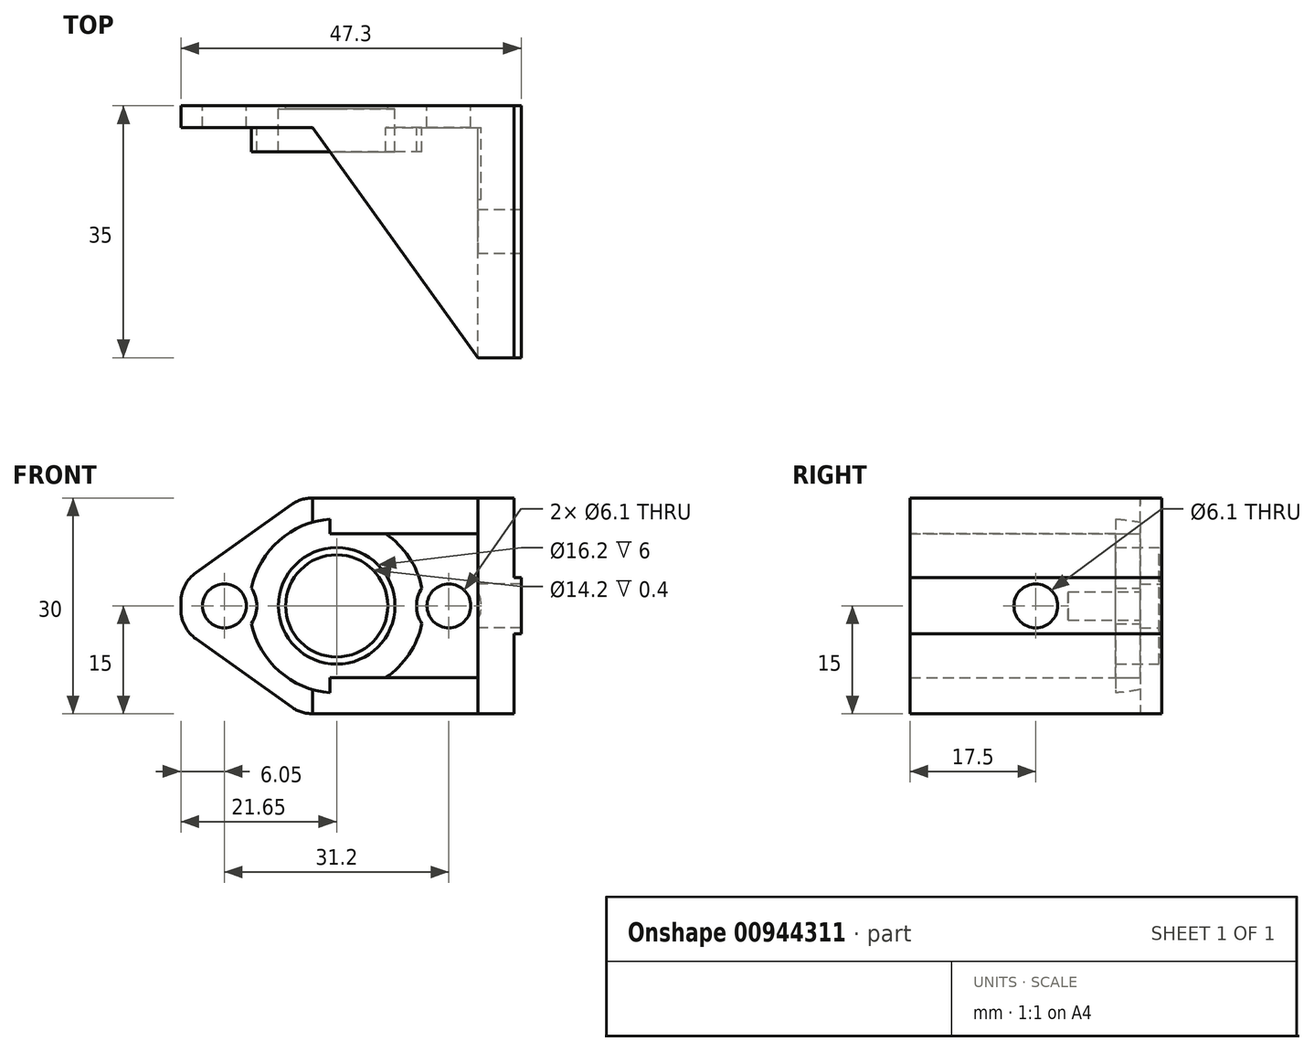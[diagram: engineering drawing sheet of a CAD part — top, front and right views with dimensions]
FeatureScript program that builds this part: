
annotation { "Feature Type Name" : "Feature", "Feature Type Description" : "" }
export const myFeature = defineFeature(function(context is Context, id is Id, definition is map)
    precondition{}
    {
        {
            var Q0;
            Q0=qCreatedBy(makeId("Front.planeOp"),FACE);
            var sketch = newSketch(context, id + "F0", { "sketchPlane" : qUnion([Q0])});
            skLineSegment(sketch, "E0.right", {"start": v(-21.65, -0.54) * mm, "end": v(-21.65, 0.54) * mm});
            skPoint(sketch, "E0.middle", {"position": v(0, 0) * mm});
            skCircle(sketch, "E1", {"center": v(-15.6, 0) * mm, "radius": 3.05 * mm});
            skCircle(sketch, "E2.MirrorC", {"center": v(15.6, 0) * mm, "radius": 3.05 * mm});
            skCircle(sketch, "E3", {"center": v(0, 0) * mm, "radius": 8.1 * mm});
            skCircle(sketch, "E4", {"center": v(0, 0) * mm, "radius": 12.1 * mm});
            skLineSegment(sketch, "E5", {"start": v(-17.37, 2.48) * mm, "end": v(-7.02, 9.86) * mm, "construction": true});
            skLineSegment(sketch, "E6", {"start": v(-19.55, 4.61) * mm, "end": v(-6.27, 14.07) * mm});
            skPoint(sketch, "E7.visualSharp", {"position": v(-21.65, 3.12) * mm});
            skArc(sketch, "E7.filletArc", {"start": v(-19.55, 4.61) * mm, "mid": v(-21.1, 2.83) * mm, "end": v(-21.65, 0.54) * mm});
            skArc(sketch, "E8.filletArc", {"start": v(-3.37, 15) * mm, "mid": v(-4.9, 14.76) * mm, "end": v(-6.27, 14.07) * mm});
            skArc(sketch, "E9.MirrorCS", {"start": v(-19.55, -4.61) * mm, "mid": v(-21.1, -2.83) * mm, "end": v(-21.65, -0.54) * mm});
            skLineSegment(sketch, "E10.MirrorCS", {"start": v(-19.55, -4.61) * mm, "end": v(-6.27, -14.07) * mm});
            skArc(sketch, "E11.MirrorCS", {"start": v(-3.37, -15) * mm, "mid": v(-4.9, -14.76) * mm, "end": v(-6.27, -14.07) * mm});
            skPoint(sketch, "E12.orphan", {"position": v(-21.65, -15) * mm});
            skLineSegment(sketch, "E13", {"start": v(-3.37, 15) * mm, "end": v(19.65, 15) * mm});
            skLineSegment(sketch, "E14", {"start": v(19.65, 15) * mm, "end": v(19.65, -15) * mm});
            skLineSegment(sketch, "E15", {"start": v(19.65, -15) * mm, "end": v(-3.37, -15) * mm});
            skLineSegment(sketch, "E16.bottom", {"start": v(19.65, 15) * mm, "end": v(24.65, 15) * mm});
            skLineSegment(sketch, "E16.top", {"start": v(19.65, -15) * mm, "end": v(24.65, -15) * mm});
            skLineSegment(sketch, "E16.right", {"start": v(24.65, 15) * mm, "end": v(24.65, -15) * mm});
            skSolve(sketch);
        }
        {
            var Q0;
            Q0=makeQuery(id+"F0.imprint","IMPRINT",FACE,{"disambiguationData":[TD([[makeQuery(id+"F0.imprint","IMPRINT",EDGE,{"derivedFrom":sQuery(id+"F0.wireOp",EDGE,"E3")}),-1.0]])]});
            extrude(context, id + "F1", {"entities" : qUnion([Q0]), "depth" : 6.4 * mm, "offsetDistance" : 25 * mm});
        }
        {
            var Q0;
            Q0=qSketchRegion(id+"F0",true);
            extrude(context, id + "F2", {"entities" : qUnion([Q0]), "operationType" : NewBodyOperationType.ADD, "depth" : 3 * mm, "offsetDistance" : 25 * mm});
        }
        {
            var Q0;
            {var subQ0=sQuery(id+"F0.wireOp",EDGE,"E4");Q0=makeQuery(id+"F2.boolean.opBoolean","MERGE",FACE,{"derivedFrom":[makeQuery(id+"F1.opExtrude","CAP_FACE",FACE,{"disambiguationData":[OSD([sQuery(id+"F0.wireOp",EDGE,"E3"),subQ0])],"isStart":true}),makeQuery(id+"F2.opExtrude","CAP_FACE",FACE,{"disambiguationData":[OSD([sQuery(id+"F0.wireOp",EDGE,"E0.bottom"),sQuery(id+"F0.wireOp",EDGE,"E0.top"),sQuery(id+"F0.wireOp",EDGE,"E0.left"),sQuery(id+"F0.wireOp",EDGE,"E0.right"),sQuery(id+"F0.wireOp",EDGE,"E1"),sQuery(id+"F0.wireOp",EDGE,"E2.MirrorC"),subQ0,sQuery(id+"F0.wireOp",EDGE,"E6"),sQuery(id+"F0.wireOp",EDGE,"E7.filletArc"),sQuery(id+"F0.wireOp",EDGE,"E8.filletArc"),sQuery(id+"F0.wireOp",EDGE,"a1945099-096e-447e-bc1c-ab5cae43a46e0.MirrorCS"),sQuery(id+"F0.wireOp",EDGE,"e7613415-c0dd-44c2-a091-62de6971341e0.MirrorCS"),sQuery(id+"F0.wireOp",EDGE,"568613a7-9c33-49a0-9674-28169e1cce0e0.MirrorCS"),sQuery(id+"F0.wireOp",EDGE,"E9.MirrorCS"),sQuery(id+"F0.wireOp",EDGE,"E10.MirrorCS"),sQuery(id+"F0.wireOp",EDGE,"E11.MirrorCS"),sQuery(id+"F0.wireOp",EDGE,"7480bcef-4817-4377-8283-0c3d8621cf620.MirrorCS"),sQuery(id+"F0.wireOp",EDGE,"9ec5c487-3746-435e-b199-95de8daa40a20.MirrorCS"),sQuery(id+"F0.wireOp",EDGE,"8ba82cc5-7c4e-43a8-960a-3daafe53bb050.MirrorCS")])],"isStart":true})]});}
            var sketch = newSketch(context, id + "F3", { "sketchPlane" : qUnion([Q0])});
            skCircle(sketch, "E17", {"center": v(0, 0) * mm, "radius": 7.1 * mm});
            skSolve(sketch);
        }
        {
            var Q0;
            Q0=makeQuery(id+"F3.imprint","IMPRINT",FACE,{"disambiguationData":[TD([[makeQuery(id+"F3.imprint","IMPRINT",EDGE,{"derivedFrom":sQuery(id+"F3.wireOp",EDGE,"E17")}),-1.0]])]});
            extrude(context, id + "F4", {"entities" : qUnion([Q0]), "operationType" : NewBodyOperationType.ADD, "oppositeDirection" : true, "depth" : 0.4 * mm, "offsetDistance" : 25 * mm});
        }
        {
            var Q0;
            Q0=makeQuery(id+"F0.imprint","IMPRINT",FACE,{"disambiguationData":[TD([[makeQuery(id+"F0.imprint","IMPRINT",EDGE,{"derivedFrom":sQuery(id+"F0.wireOp",EDGE,"E16.bottom")}),-1.0]])]});
            extrude(context, id + "F5", {"entities" : qUnion([Q0]), "operationType" : NewBodyOperationType.ADD, "depth" : 35 * mm, "offsetDistance" : 25 * mm});
        }
        {
            var Q0;
            Q0=makeQuery(id+"F2.opExtrude","CAP_FACE",FACE,{"disambiguationData":[OSD([sQuery(id+"F0.wireOp",EDGE,"E0.right"),sQuery(id+"F0.wireOp",EDGE,"E1"),sQuery(id+"F0.wireOp",EDGE,"E2.MirrorC"),sQuery(id+"F0.wireOp",EDGE,"E4"),sQuery(id+"F0.wireOp",EDGE,"E6"),sQuery(id+"F0.wireOp",EDGE,"E7.filletArc"),sQuery(id+"F0.wireOp",EDGE,"E8.filletArc"),sQuery(id+"F0.wireOp",EDGE,"E9.MirrorCS"),sQuery(id+"F0.wireOp",EDGE,"E10.MirrorCS"),sQuery(id+"F0.wireOp",EDGE,"E11.MirrorCS"),sQuery(id+"F0.wireOp",EDGE,"E13"),sQuery(id+"F0.wireOp",EDGE,"E15"),sQuery(id+"F0.wireOp",EDGE,"E16.bottom"),sQuery(id+"F0.wireOp",EDGE,"E16.top"),sQuery(id+"F0.wireOp",EDGE,"E16.right")])],"isStart":false});
            var sketch = newSketch(context, id + "F6", { "sketchPlane" : qUnion([Q0])});
            skLineSegment(sketch, "E18", {"start": v(-0.37, 0) * mm, "end": v(28.02, 0) * mm, "construction": true});
            skLineSegment(sketch, "E19", {"start": v(15.6, 0) * mm, "end": v(15.6, -7.1) * mm, "construction": true});
            skLineSegment(sketch, "E20", {"start": v(0, 0) * mm, "end": v(-25.26, 0) * mm, "construction": true});
            skLineSegment(sketch, "E21", {"start": v(-15.6, 0) * mm, "end": v(-15.6, -7.65) * mm, "construction": true});
            skCircle(sketch, "E22", {"center": v(-15.6, 0) * mm, "radius": 4.5 * mm});
            skCircle(sketch, "E23", {"center": v(15.6, 0) * mm, "radius": 4.5 * mm});
            skSolve(sketch);
        }
        {
            var Q0;
            Q0=qSketchRegion(id+"F6",true);
            extrude(context, id + "F7", {"entities" : qUnion([Q0]), "operationType" : NewBodyOperationType.REMOVE, "depth" : 10 * mm, "offsetDistance" : 25 * mm});
        }
        {
            var Q0;
            {var subQ0=sQuery(id+"F0.wireOp",EDGE,"E16.top");Q0=makeQuery(id+"F5.boolean.opBoolean","MERGE",FACE,{"derivedFrom":[makeQuery(id+"F2.opExtrude","SWEPT_FACE",FACE,{"disambiguationData":[OSD([sQuery(id+"F0.wireOp",EDGE,"E15"),subQ0])]}),makeQuery(id+"F5.opExtrude","SWEPT_FACE",FACE,{"disambiguationData":[OSD([subQ0])]})]});}
            var sketch = newSketch(context, id + "F8", { "sketchPlane" : qUnion([Q0])});
            skLineSegment(sketch, "E24", {"start": v(19.65, 35) * mm, "end": v(-3.37, 3) * mm});
            skLineSegment(sketch, "E25", {"start": v(-3.37, 3) * mm, "end": v(19.65, 3) * mm});
            skLineSegment(sketch, "E26", {"start": v(19.65, 3) * mm, "end": v(19.65, 35) * mm});
            skSolve(sketch);
        }
        {
            var Q0;
            Q0=makeQuery(id+"F8.imprint","IMPRINT",FACE,{"disambiguationData":[TD([[makeQuery(id+"F8.imprint","IMPRINT",EDGE,{"derivedFrom":sQuery(id+"F8.wireOp",EDGE,"E24")}),1.0]])]});
            extrude(context, id + "F9", {"entities" : qUnion([Q0]), "operationType" : NewBodyOperationType.ADD, "oppositeDirection" : true, "depth" : 5 * mm, "offsetDistance" : 25 * mm});
        }
        {
            var Q0;
            {var subQ0=sQuery(id+"F0.wireOp",EDGE,"E16.bottom");Q0=makeQuery(id+"F5.boolean.opBoolean","MERGE",FACE,{"derivedFrom":[makeQuery(id+"F2.opExtrude","SWEPT_FACE",FACE,{"disambiguationData":[OSD([sQuery(id+"F0.wireOp",EDGE,"E13"),subQ0])]}),makeQuery(id+"F5.opExtrude","SWEPT_FACE",FACE,{"disambiguationData":[OSD([subQ0])]})]});}
            var sketch = newSketch(context, id + "F10", { "sketchPlane" : qUnion([Q0])});
            skLineSegment(sketch, "E27", {"start": v(-3.37, -3) * mm, "end": v(19.65, -35) * mm});
            skLineSegment(sketch, "E28", {"start": v(19.65, -35) * mm, "end": v(19.65, -3) * mm});
            skLineSegment(sketch, "E29", {"start": v(19.65, -3) * mm, "end": v(-3.37, -3) * mm});
            skSolve(sketch);
        }
        {
            var Q0;
            Q0=makeQuery(id+"F10.imprint","IMPRINT",FACE,{"disambiguationData":[TD([[makeQuery(id+"F10.imprint","IMPRINT",EDGE,{"derivedFrom":sQuery(id+"F10.wireOp",EDGE,"E27")}),1.0]])]});
            extrude(context, id + "F11", {"entities" : qUnion([Q0]), "operationType" : NewBodyOperationType.ADD, "oppositeDirection" : true, "depth" : 5 * mm, "offsetDistance" : 25 * mm});
        }
        {
            var Q0;
            {var subQ0=sQuery(id+"F0.wireOp",EDGE,"E16.right");Q0=makeQuery(id+"F5.boolean.opBoolean","MERGE",FACE,{"derivedFrom":[makeQuery(id+"F2.opExtrude","SWEPT_FACE",FACE,{"disambiguationData":[OSD([subQ0])]}),makeQuery(id+"F5.opExtrude","SWEPT_FACE",FACE,{"disambiguationData":[OSD([subQ0])]})]});}
            var sketch = newSketch(context, id + "F12", { "sketchPlane" : qUnion([Q0])});
            skLineSegment(sketch, "E30", {"start": v(0, 0) * mm, "end": v(-35, 0) * mm, "construction": true});
            skLineSegment(sketch, "E31.bottom", {"start": v(0, 3.9) * mm, "end": v(-35, 3.9) * mm});
            skLineSegment(sketch, "E31.top", {"start": v(0, -3.9) * mm, "end": v(-35, -3.9) * mm});
            skLineSegment(sketch, "E31.left", {"start": v(0, 3.9) * mm, "end": v(0, -3.9) * mm});
            skLineSegment(sketch, "E31.right", {"start": v(-35, 3.9) * mm, "end": v(-35, -3.9) * mm});
            skPoint(sketch, "E31.middle", {"position": v(-17.5, 0) * mm});
            skCircle(sketch, "E32", {"center": v(-17.5, 0) * mm, "radius": 3.05 * mm});
            skSolve(sketch);
        }
        {
            var Q0;
            Q0=makeQuery(id+"F12.imprint","IMPRINT",FACE,{"disambiguationData":[TD([[makeQuery(id+"F12.imprint","IMPRINT",EDGE,{"derivedFrom":sQuery(id+"F12.wireOp",EDGE,"E31.bottom")}),1.0]])]});
            extrude(context, id + "F13", {"entities" : qUnion([Q0]), "operationType" : NewBodyOperationType.ADD, "depth" : 1 * mm, "offsetDistance" : 25 * mm});
        }
        {
            var Q0;
            {var subQ0=sQuery(id+"F0.wireOp",EDGE,"E16.right");Q0=makeQuery(id+"F13.boolean.opBoolean","SPLIT",FACE,{"disambiguationData":[TD([makeQuery(id+"F13.opExtrude","SWEPT_FACE",FACE,{"disambiguationData":[OSD([sQuery(id+"F12.wireOp",EDGE,"E32")])]})])],"derivedFrom":makeQuery(id+"F5.boolean.opBoolean","MERGE",FACE,{"derivedFrom":[makeQuery(id+"F2.opExtrude","SWEPT_FACE",FACE,{"disambiguationData":[OSD([subQ0])]}),makeQuery(id+"F5.opExtrude","SWEPT_FACE",FACE,{"disambiguationData":[OSD([subQ0])]})]})});}
            extrude(context, id + "F14", {"entities" : qUnion([Q0]), "operationType" : NewBodyOperationType.REMOVE, "endBound" : BoundingType.THROUGH_ALL, "oppositeDirection" : true, "depth" : 25 * mm, "offsetDistance" : 25 * mm});
        }
    });
